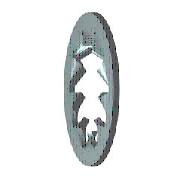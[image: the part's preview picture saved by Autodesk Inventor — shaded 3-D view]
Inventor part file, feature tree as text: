
AUTODESK INVENTOR PART (.ipt)
format: ipt  version: 2021 (Build 250183000, 183)  size: 159,232 bytes
history: native  units: mm (DEFAULTED — no unit token found)
features: sketch x2, extrude x1, pattern_circular x1, plane x1
ambient origin geometry x7: Origin, YZ Plane, XY Plane, X Axis, Y Axis, Z Axis, Center Point
bodies: Solid1 (feature_tree), Body (feature_tree)
feature tree (5):
  extrude  "Cut"  Depth=3.2mm
  pattern_circular  "Cuts"  [2 undecoded]
  plane  "Work Plane1"
  sketch  "Sketch1"  dims[d0=6.0mm d1=3.2mm]
  sketch  "Sketch2"  dims[d2=0.4mm d3=0.0mm d4=4.6mm d5=15.0deg d6=0.4mm d7=0.0mm d8=0.096mm d9=60.0mm d11=360.0deg d12=0.0mm d13=0.0mm d18=0.0mm d19=0.0mm]
note: 2 required parameter values undecoded (feature->parameter linkage not recoverable at this tier; creation-order binding heuristic only, values carry confidence <= 0.55)
